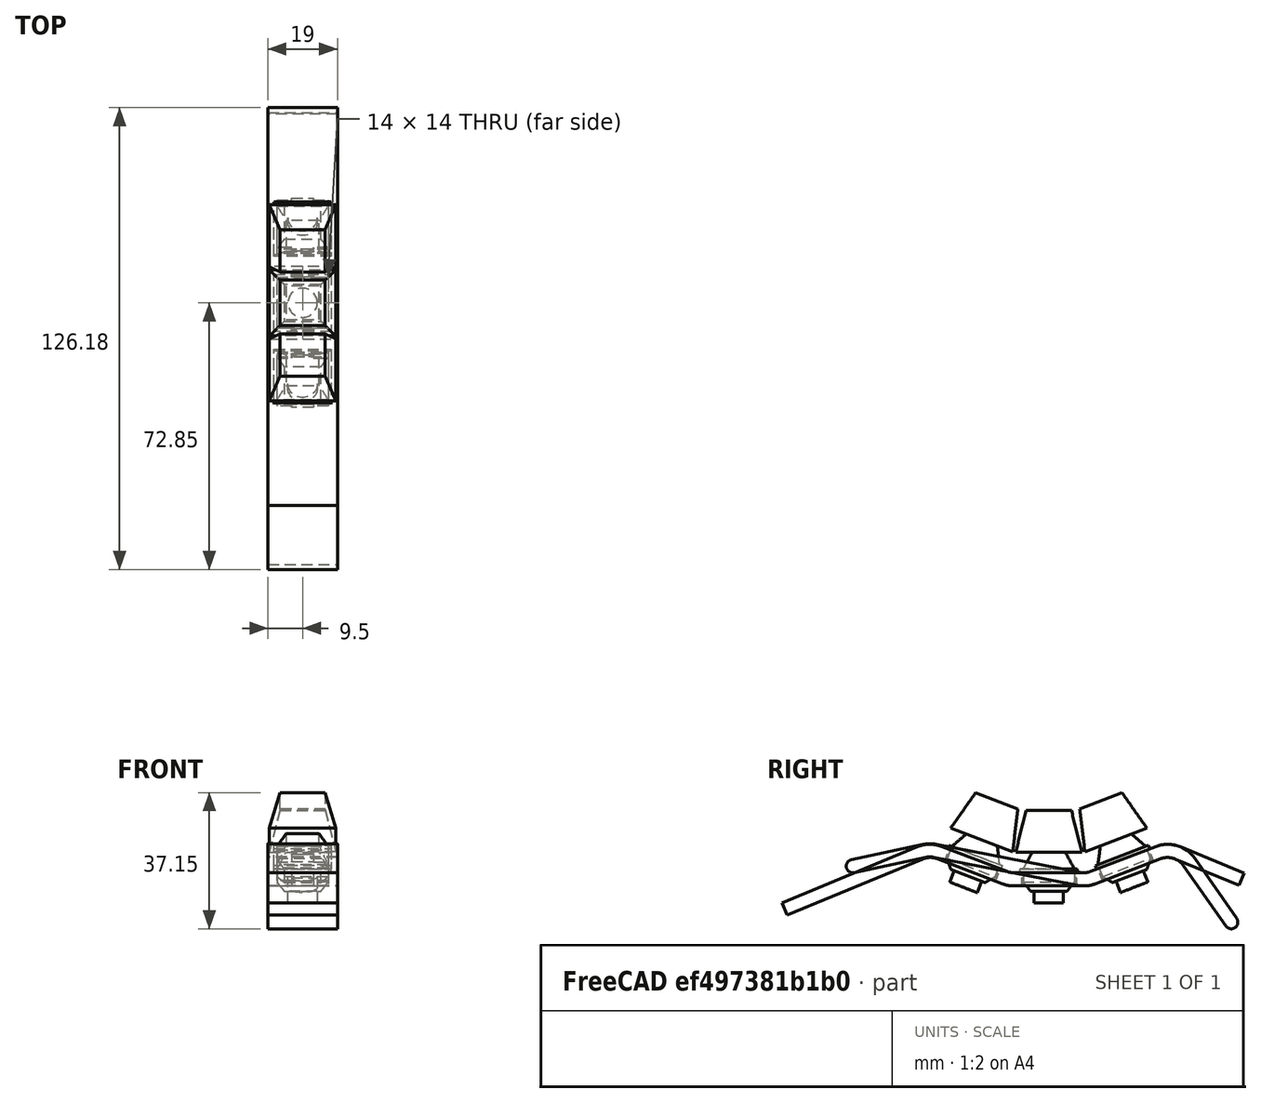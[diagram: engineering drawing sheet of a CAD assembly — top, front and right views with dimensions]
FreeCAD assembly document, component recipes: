
FREECAD ASSEMBLY — COMPONENT RECIPES ("KeyColumn2")

This assembly document has 4 components, labeled P0..P3 below (a component is one placed body or linked part). 2 of them carry a construction recipe — the FreeCAD feature program that regenerates the part from scratch, quoted from this document or its linked companion documents; the rest are supplied as boundary geometry only. No exploded tour is included for this assembly.
COMPONENT P0 — recipe-attached ("TrimA", modeled in this document).
Construction recipe (the document's own serialized feature program — sketch geometry with constraints, then the solid features built on it; lengths are millimeters unless a unit is written):

FEATURE [PartDesign::SubShapeBinder] Binder
  BindCopyOnChange = 0
  BindMode = 0
  ClaimChildren = false
  Context = -> Body003 [Binder.]
  Fuse = false
  MakeFace = true
  OffsetFill = false
  OffsetIntersection = false
  OffsetJoinType = 0
  OffsetOpenResult = false
  PartialLoad = false
  Relative = true
  Support = -> [Extrude001[Face21]]
  _Version = 2
FEATURE [Sketcher::SketchObject] Sketch002
  ExternalGeometry = -> [Binder]
  FullyConstrained = true
  MapMode = 5
  Placement = pos=(0,0,0) rot=(0.57735,0.57735,0.57735;2.0944rad)
  Support = -> [YZ_Plane003]
  sketch-geometry (4):
    g0: LineSegment StartX=53.3288 StartY=1.66298 StartZ=0 EndX=56.6547 EndY=0.285323 EndZ=0
    g1: LineSegment StartX=56.6547 StartY=0.285323 StartZ=0 EndX=55.2771 EndY=-3.04064 EndZ=0
    g2: LineSegment StartX=55.2771 StartY=-3.04064 StartZ=0 EndX=51.9511 EndY=-1.66298 EndZ=0
    g3: LineSegment StartX=51.9511 StartY=-1.66298 StartZ=0 EndX=53.3288 EndY=1.66298 EndZ=0
  constraints (10):
    c: Coincident(g0,g-3)
    c: Coincident(g0,g1)
    c: Coincident(g1,g2)
    c: Coincident(g2,g-4)
    c: Coincident(g2,g3)
    c: Coincident(g3,g0)
    c: Perpendicular(g0,g3)
    c: Perpendicular(g2,g3)
    c: Perpendicular(g1,g2)
    c: Equal(g3,g0)
FEATURE [PartDesign::Pad] Pad
  Direction = (1,-2e-16,3e-16)
  Length = 20
  Length2 = 10
  Midplane = true
  Placement = pos=(0,0,0) rot=(0.57735,0.57735,0.57735;2.0944rad)
  Profile = -> Sketch002
  ReferenceAxis = -> Sketch002 [N_Axis]
  Type = 0
FEATURE [PartDesign::Body] Body003  label="TrimA"
  Group = -> [Binder,Sketch002,Pad]
  Origin = -> Origin003
  Tip = -> Pad
COMPONENT P1 — recipe-attached ("TrimB", modeled in this document).
Construction recipe (the document's own serialized feature program — sketch geometry with constraints, then the solid features built on it; lengths are millimeters unless a unit is written):

FEATURE [PartDesign::SubShapeBinder] Binder001
  BindCopyOnChange = 0
  BindMode = 0
  ClaimChildren = false
  Context = -> Body004 [Binder001.]
  Fuse = false
  MakeFace = true
  OffsetFill = false
  OffsetIntersection = false
  OffsetJoinType = 0
  OffsetOpenResult = false
  PartialLoad = false
  Relative = true
  _Version = 2
FEATURE [Sketcher::SketchObject] Sketch003
  ExternalGeometry = -> [Binder001]
  FullyConstrained = true
  MapMode = 5
  Placement = pos=(0,0,0) rot=(0.57735,0.57735,0.57735;2.0944rad)
  Support = -> [YZ_Plane004]
  sketch-geometry (4):
    g0: LineSegment StartX=-72.8528 StartY=-6.42415 StartZ=0 EndX=-71.4752 EndY=-9.75012 EndZ=0
    g1: LineSegment StartX=-71.4752 StartY=-9.75012 StartZ=0 EndX=-74.8011 EndY=-11.1278 EndZ=0
    g2: LineSegment StartX=-74.8011 StartY=-11.1278 StartZ=0 EndX=-76.1788 EndY=-7.80181 EndZ=0
    g3: LineSegment StartX=-76.1788 StartY=-7.80181 StartZ=0 EndX=-72.8528 EndY=-6.42415 EndZ=0
  constraints (10):
    c: Coincident(g0,g-3)
    c: Coincident(g0,g-4)
    c: Coincident(g0,g1)
    c: Coincident(g1,g2)
    c: Coincident(g2,g3)
    c: Coincident(g3,g0)
    c: Perpendicular(g0,g3)
    c: Perpendicular(g0,g1)
    c: Perpendicular(g1,g2)
    c: Equal(g0,g1)
FEATURE [PartDesign::Pad] Pad001
  Direction = (1,-2e-16,3e-16)
  Length = 20
  Length2 = 10
  Midplane = true
  Placement = pos=(0,0,0) rot=(0.57735,0.57735,0.57735;2.0944rad)
  Profile = -> Sketch003
  ReferenceAxis = -> Sketch003 [N_Axis]
  Type = 0
FEATURE [PartDesign::SubShapeBinder] Binder002
  BindCopyOnChange = 0
  BindMode = 0
  ClaimChildren = false
  Context = -> Body004 [Binder002.]
  Fuse = false
  MakeFace = true
  OffsetFill = false
  OffsetIntersection = false
  OffsetJoinType = 0
  OffsetOpenResult = false
  PartialLoad = false
  Relative = true
  Support = -> [Extrude001[Face21]]
  _Version = 2
FEATURE [PartDesign::Body] Body004  label="TrimB"
  Group = -> [Binder001,Sketch003,Pad001,Binder002]
  Origin = -> Origin004
  Tip = -> Pad001
COMPONENT P2 — geometry summary ("MXSwitch100Nice002"; no construction recipe available for this part):
  bounding box: 27.3 x 19.3 x 18.1 mm
  tessellated surface: 588 triangles
  volume: 4560 mm^3 (48% of its bounding box)
  symmetry: mirror-symmetric across its x mid-plane
COMPONENT P3 — geometry summary ("MX-Latch-Subtractor2N002"; no construction recipe available for this part):
  bounding box: 17.1 x 14.5 x 14.0 mm
  tessellated surface: 44 triangles
  volume: 2012 mm^3 (58% of its bounding box)
PROVENANCE & LICENSES
A FreeCAD (.FCStd) document from a public repository crawl; recipes are the document's own serialized feature recipes (and, for linked parts, companion documents' recipes).
License: mit.
